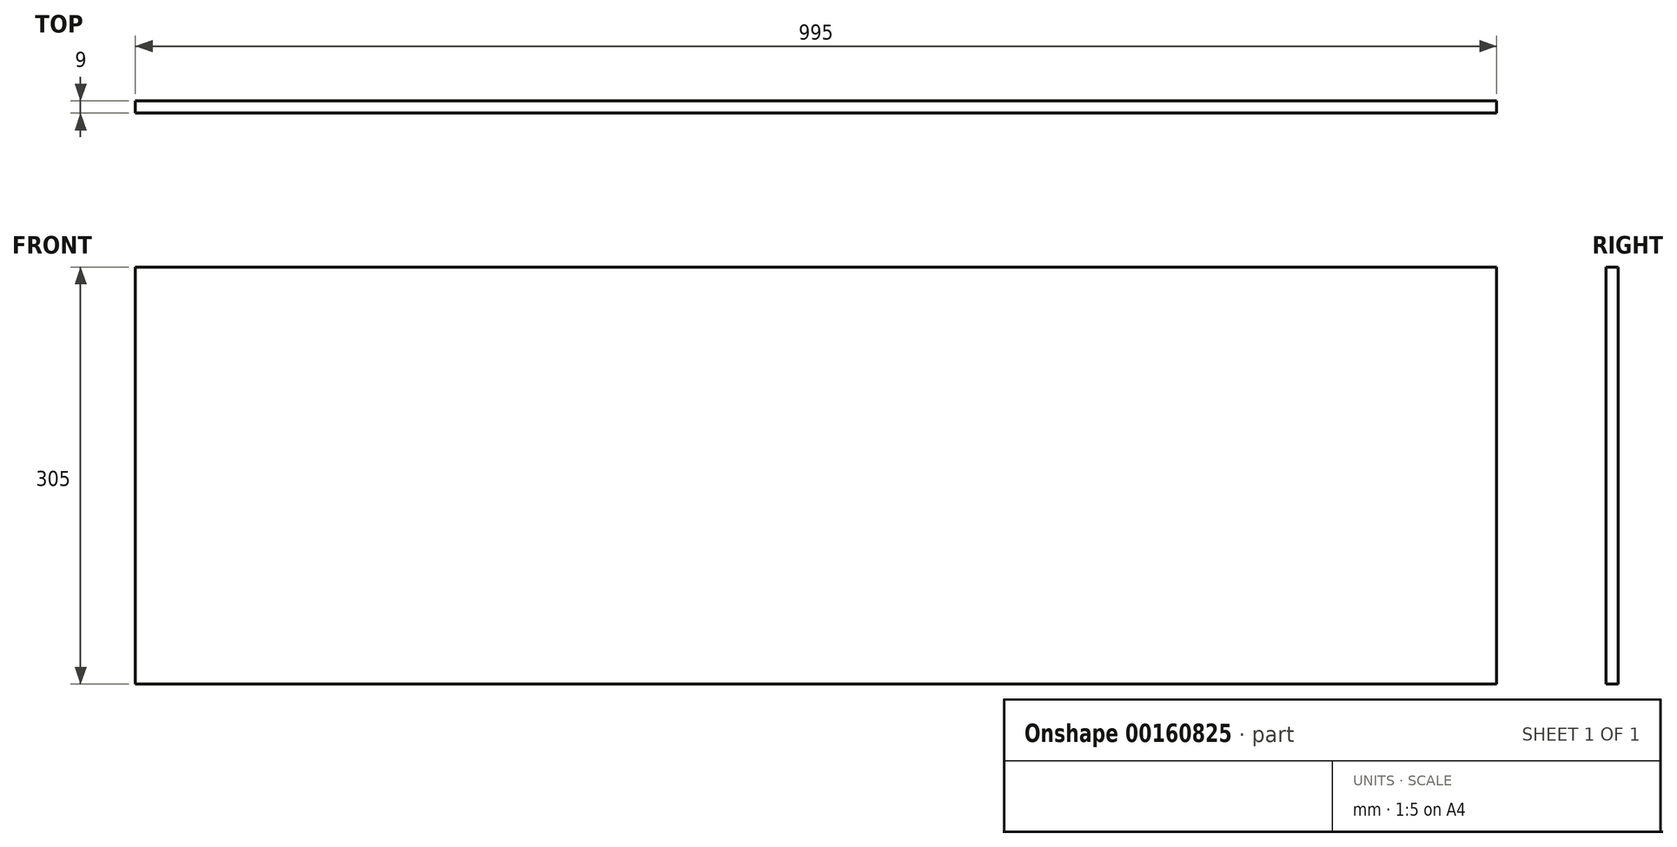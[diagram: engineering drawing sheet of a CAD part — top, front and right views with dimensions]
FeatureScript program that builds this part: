
annotation { "Feature Type Name" : "Feature", "Feature Type Description" : "" }
export const myFeature = defineFeature(function(context is Context, id is Id, definition is map)
    precondition{}
    {
        {
            var Q0;
            Q0=qCreatedBy(makeId("Front.planeOp"),FACE);
            var sketch = newSketch(context, id + "F0", { "sketchPlane" : qUnion([Q0])});
            skLineSegment(sketch, "E0.bottom", {"start": v(2.57, 0) * mm, "end": v(997.57, 0) * mm});
            skLineSegment(sketch, "E0.top", {"start": v(2.57, 305) * mm, "end": v(997.57, 305) * mm});
            skLineSegment(sketch, "E0.left", {"start": v(2.57, 0) * mm, "end": v(2.57, 305) * mm});
            skLineSegment(sketch, "E0.right", {"start": v(997.57, 0) * mm, "end": v(997.57, 305) * mm});
            skSolve(sketch);
        }
        {
            var Q0;
            Q0=qSketchRegion(id+"F0",true);
            extrude(context, id + "F1", {"entities" : qUnion([Q0]), "depth" : 9 * mm});
        }
    });
